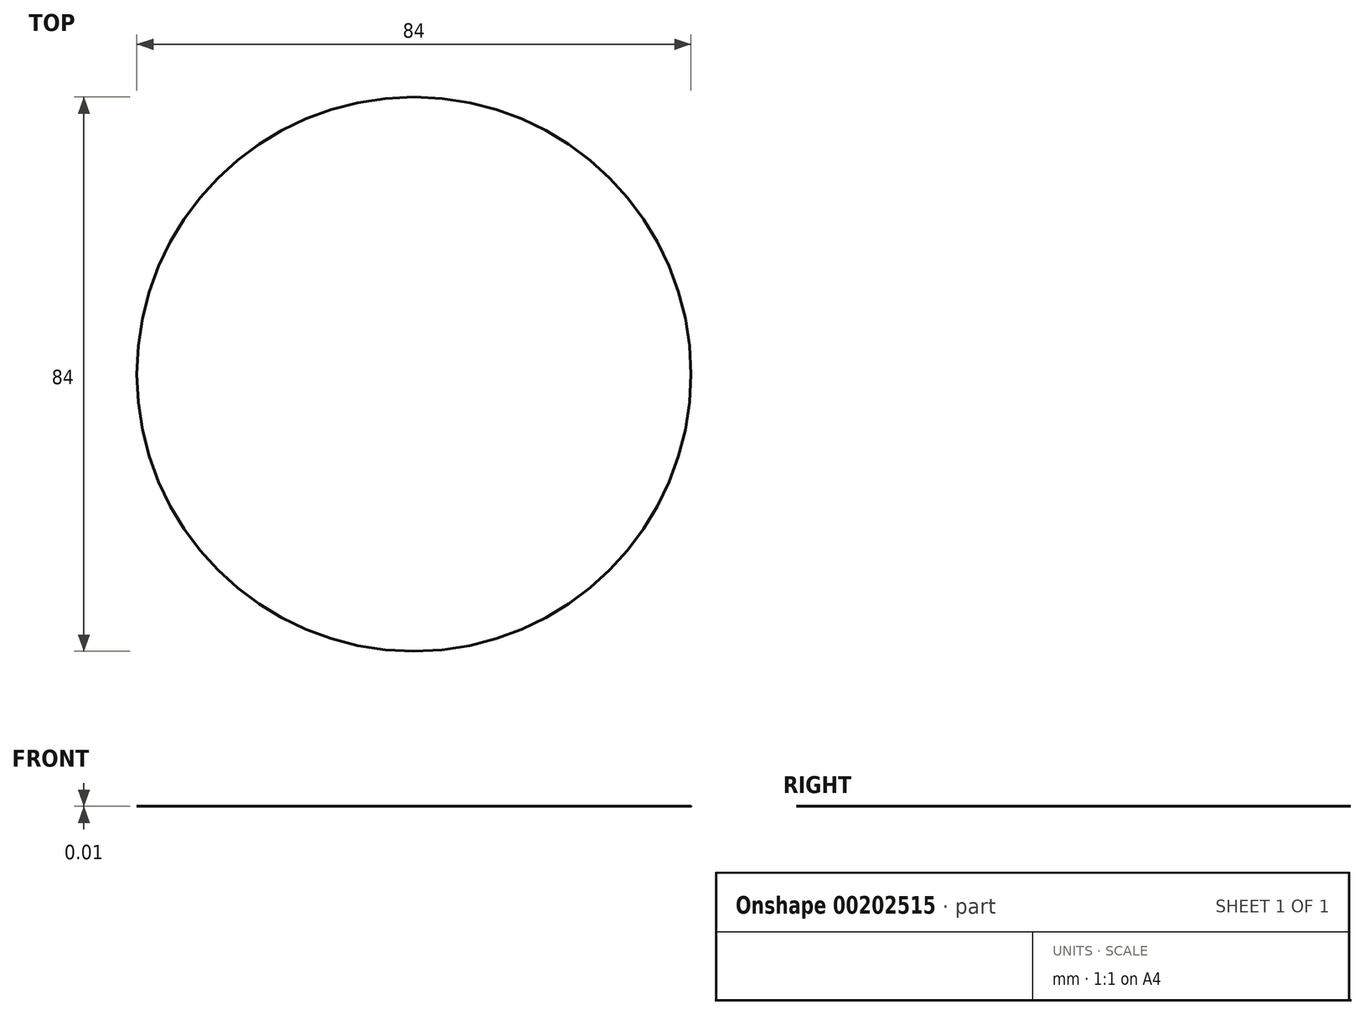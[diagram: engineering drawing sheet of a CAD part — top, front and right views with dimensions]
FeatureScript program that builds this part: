
annotation { "Feature Type Name" : "Feature", "Feature Type Description" : "" }
export const myFeature = defineFeature(function(context is Context, id is Id, definition is map)
    precondition{}
    {
        {
            var Q0;
            Q0=qCreatedBy(makeId("Top.planeOp"),FACE);
            var sketch = newSketch(context, id + "F0", { "sketchPlane" : qUnion([Q0])});
            skCircle(sketch, "E0", {"center": v(0, 0) * mm, "radius": 42 * mm});
            skSolve(sketch);
        }
        {
            var Q0;
            Q0 = qSketchRegion(id + "F0", true);
            extrude(context, id + "F1", {"entities" : qUnion([Q0]), "depth" : 0.01 * mm});
        }
    });
